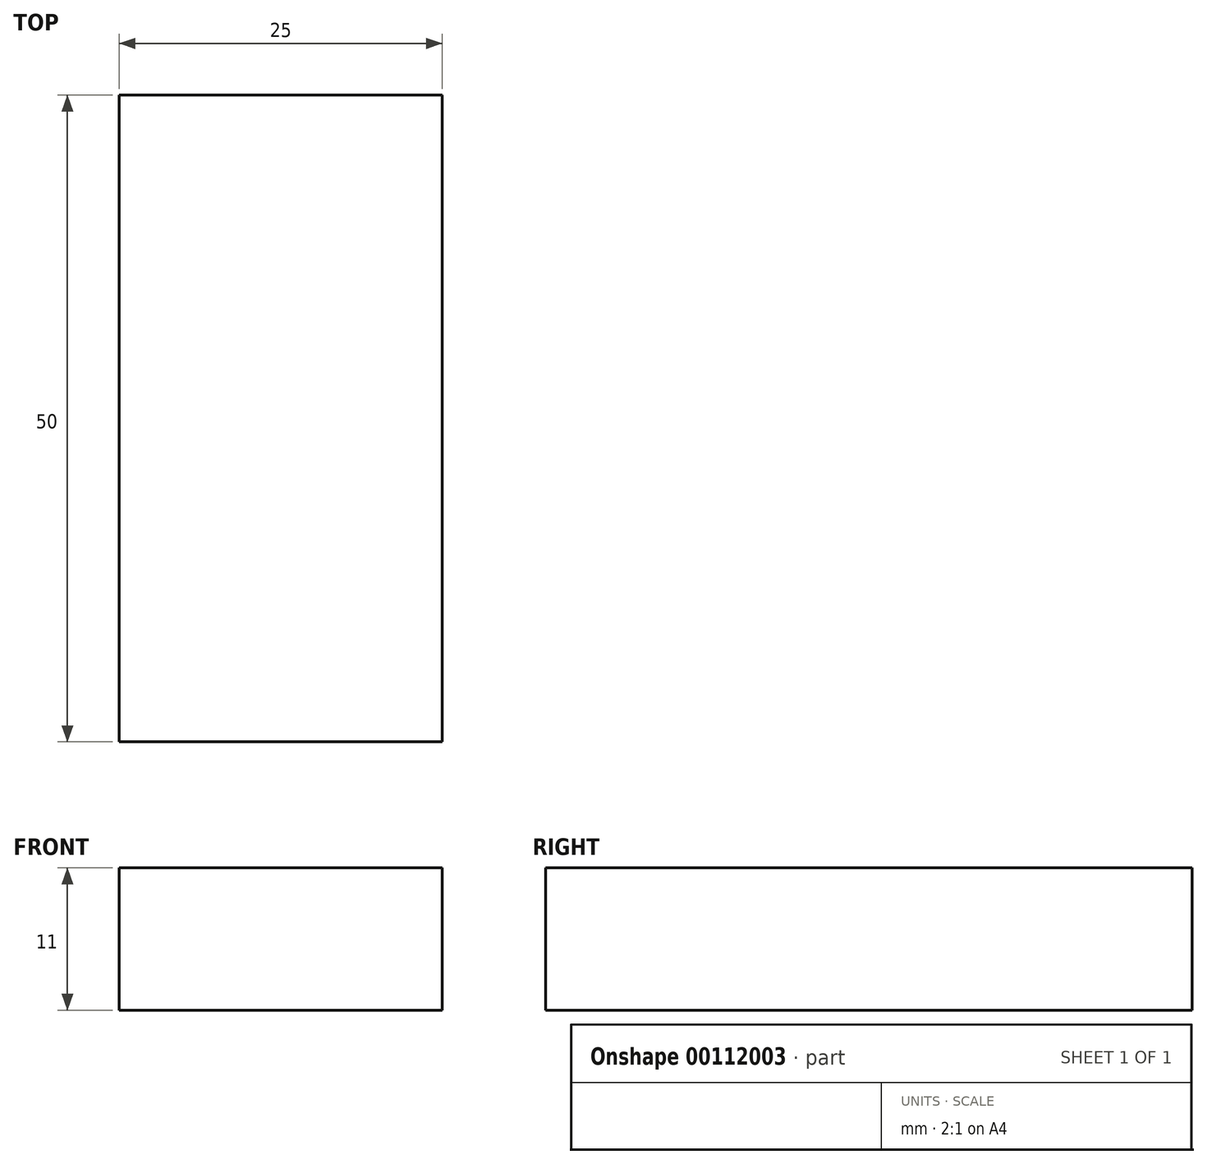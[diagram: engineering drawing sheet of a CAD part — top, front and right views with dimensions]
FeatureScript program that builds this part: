
annotation { "Feature Type Name" : "Feature", "Feature Type Description" : "" }
export const myFeature = defineFeature(function(context is Context, id is Id, definition is map)
    precondition{}
    {
        {
            var Q0;
            Q0=qCreatedBy(makeId("Top.planeOp"),FACE);
            var sketch = newSketch(context, id + "F0", { "sketchPlane" : qUnion([Q0])});
            skLineSegment(sketch, "E0.bottom", {"start": v(0, 0) * mm, "end": v(25, 0) * mm});
            skLineSegment(sketch, "E0.top", {"start": v(0, -50) * mm, "end": v(25, -50) * mm});
            skLineSegment(sketch, "E0.left", {"start": v(0, 0) * mm, "end": v(0, -50) * mm});
            skLineSegment(sketch, "E0.right", {"start": v(25, 0) * mm, "end": v(25, -50) * mm});
            skSolve(sketch);
        }
        {
            var Q0;
            Q0 = qSketchRegion(id + "F0", true);
            extrude(context, id + "F1", {"entities" : qUnion([Q0]), "depth" : 11 * mm});
        }
    });
